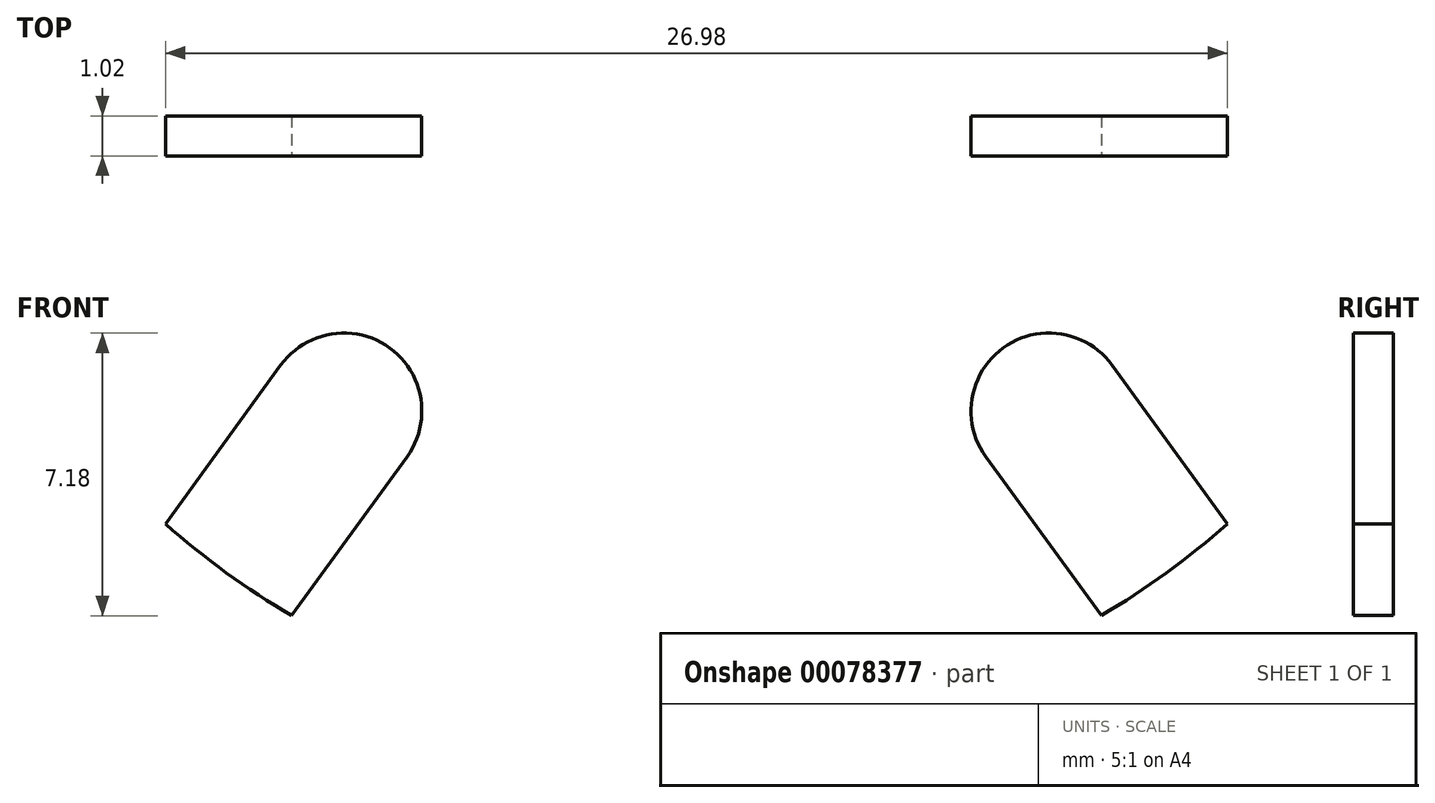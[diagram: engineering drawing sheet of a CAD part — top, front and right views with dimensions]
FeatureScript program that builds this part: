
annotation { "Feature Type Name" : "Feature", "Feature Type Description" : "" }
export const myFeature = defineFeature(function(context is Context, id is Id, definition is map)
    precondition{}
    {
        {
            var Q0;
            Q0=qCreatedBy(makeId("Front.planeOp"),FACE);
            var sketch = newSketch(context, id + "F0", { "sketchPlane" : qUnion([Q0])});
            skCircle(sketch, "E0", {"center": v(0, 0) * mm, "radius": 20.32 * mm});
            skCircle(sketch, "E1", {"center": v(0, 0) * mm, "radius": 4.06 * mm});
            skSolve(sketch);
        }
        {
            var Q0;
            Q0 = qSketchRegion(id + "F0", true);
            extrude(context, id + "F1", {"entities" : qUnion([Q0]), "endBound" : BoundingType.SYMMETRIC, "depth" : 1.02 * mm});
        }
        {
            var Q0;
            Q0=makeQuery(id+"F1.opExtrude","CAP_FACE",FACE,{"disambiguationData":[OSD([sQuery(id+"F0.wireOp",EDGE,"E0")])],"isStart":false});
            var sketch = newSketch(context, id + "F2", { "sketchPlane" : qUnion([Q0])});
            skCircle(sketch, "E2", {"center": v(0, 0) * mm, "radius": 20.32 * mm, "construction": true});
            skLineSegment(sketch, "E3", {"start": v(0, 0) * mm, "end": v(17.18, -23.65) * mm, "construction": true});
            skLineSegment(sketch, "E4", {"start": v(0, 0) * mm, "end": v(26.95, 8.76) * mm, "construction": true});
            skLineSegment(sketch, "E5", {"start": v(0, 0) * mm, "end": v(12.6, 4.1) * mm, "construction": true});
            skArc(sketch, "E6", {"start": v(13.88, 6.6) * mm, "mid": v(12.73, 5.6) * mm, "end": v(12.6, 4.1) * mm});
            skLineSegment(sketch, "E7", {"start": v(13.88, 6.6) * mm, "end": v(19.16, 8.3) * mm});
            skLineSegment(sketch, "E8", {"start": v(19.16, 8.3) * mm, "end": v(19.77, 6.42) * mm});
            skLineSegment(sketch, "E9.MirrorCS", {"start": v(15.1, 2.83) * mm, "end": v(20.38, 4.54) * mm});
            skArc(sketch, "E10.MirrorCS", {"start": v(15.1, 2.83) * mm, "mid": v(13.6, 2.94) * mm, "end": v(12.6, 4.1) * mm});
            skLineSegment(sketch, "E11.MirrorCS", {"start": v(20.38, 4.54) * mm, "end": v(19.77, 6.42) * mm});
            skLineSegment(sketch, "E12.1.0", {"start": v(13.82, -15.65) * mm, "end": v(12.22, -16.82) * mm});
            skLineSegment(sketch, "E12.1.1", {"start": v(10.56, -11.16) * mm, "end": v(13.82, -15.65) * mm});
            skLineSegment(sketch, "E12.1.2", {"start": v(10.62, -17.98) * mm, "end": v(12.22, -16.82) * mm});
            skLineSegment(sketch, "E12.1.3", {"start": v(7.36, -13.5) * mm, "end": v(10.62, -17.98) * mm});
            skArc(sketch, "E12.1.4", {"start": v(7.36, -13.5) * mm, "mid": v(7, -12.02) * mm, "end": v(7.8, -10.73) * mm});
            skArc(sketch, "E12.1.5", {"start": v(10.56, -11.16) * mm, "mid": v(9.27, -10.37) * mm, "end": v(7.8, -10.73) * mm});
            skLineSegment(sketch, "E12.anchor1", {"start": v(0, 0) * mm, "end": v(19.77, 6.42) * mm, "construction": true});
            skLineSegment(sketch, "E12.anchor2", {"start": v(0, 0) * mm, "end": v(12.22, -16.82) * mm, "construction": true});
            skLineSegment(sketch, "E13.MirrorCS", {"start": v(-13.88, 6.6) * mm, "end": v(-19.16, 8.3) * mm});
            skLineSegment(sketch, "E14.MirrorCS", {"start": v(-19.16, 8.3) * mm, "end": v(-19.77, 6.42) * mm});
            skLineSegment(sketch, "E15.MirrorCS", {"start": v(-20.38, 4.54) * mm, "end": v(-19.77, 6.42) * mm});
            skLineSegment(sketch, "E16.MirrorCS", {"start": v(-15.1, 2.83) * mm, "end": v(-20.38, 4.54) * mm});
            skArc(sketch, "E17.MirrorCS", {"start": v(-15.1, 2.83) * mm, "mid": v(-13.6, 2.94) * mm, "end": v(-12.6, 4.1) * mm});
            skArc(sketch, "E18.MirrorCS", {"start": v(-13.88, 6.6) * mm, "mid": v(-12.73, 5.6) * mm, "end": v(-12.6, 4.1) * mm});
            skArc(sketch, "E19.MirrorCS", {"start": v(-10.56, -11.16) * mm, "mid": v(-9.27, -10.37) * mm, "end": v(-7.8, -10.73) * mm});
            skLineSegment(sketch, "E20.MirrorCS", {"start": v(-10.56, -11.16) * mm, "end": v(-13.82, -15.65) * mm});
            skLineSegment(sketch, "E21.MirrorCS", {"start": v(-13.82, -15.65) * mm, "end": v(-12.22, -16.82) * mm});
            skLineSegment(sketch, "E22.MirrorCS", {"start": v(-10.62, -17.98) * mm, "end": v(-12.22, -16.82) * mm});
            skLineSegment(sketch, "E23.MirrorCS", {"start": v(-7.36, -13.5) * mm, "end": v(-10.62, -17.98) * mm});
            skArc(sketch, "E24.MirrorCS", {"start": v(-7.36, -13.5) * mm, "mid": v(-7, -12.02) * mm, "end": v(-7.8, -10.73) * mm});
            skSolve(sketch);
        }
        {
            var Q0;
            {var subQ5=sQuery(id+"F2.wireOp",EDGE,"E6");Q0=makeQuery(id+"F2.imprint","IMPRINT",FACE,{"disambiguationData":[TD([[makeQuery(id+"F2.imprint","IMPRINT",EDGE,{"derivedFrom":subQ5}),1.0]])]});}
            var Q1;
            {var subQ1=sQuery(id+"F2.wireOp",EDGE,"E12.1.4");Q1=makeQuery(id+"F2.imprint","IMPRINT",FACE,{"disambiguationData":[TD([[makeQuery(id+"F2.imprint","IMPRINT",EDGE,{"derivedFrom":subQ1}),-1.0]])]});}
            var Q2;
            {var subQ5=sQuery(id+"F2.wireOp",EDGE,"E19.MirrorCS");Q2=makeQuery(id+"F2.imprint","IMPRINT",FACE,{"disambiguationData":[TD([[makeQuery(id+"F2.imprint","IMPRINT",EDGE,{"derivedFrom":subQ5}),-1.0]])]});}
            var Q3;
            {var subQ1=sQuery(id+"F2.wireOp",EDGE,"E17.MirrorCS");Q3=makeQuery(id+"F2.imprint","IMPRINT",FACE,{"disambiguationData":[TD([[makeQuery(id+"F2.imprint","IMPRINT",EDGE,{"derivedFrom":subQ1}),1.0]])]});}
            var Q4;
            Q4 = qConstructionFilter(qBodyType(qCreatedBy(id + "F2" ,EDGE), BodyType.WIRE), ConstructionObject.NO);
            extrude(context, id + "F3", {"entities" : qUnion([Q0, Q1, Q2, Q3]), "operationType" : NewBodyOperationType.REMOVE, "surfaceEntities" : qUnion([Q4]), "oppositeDirection" : true, "depth" : 25.4 * mm});
        }
    });
